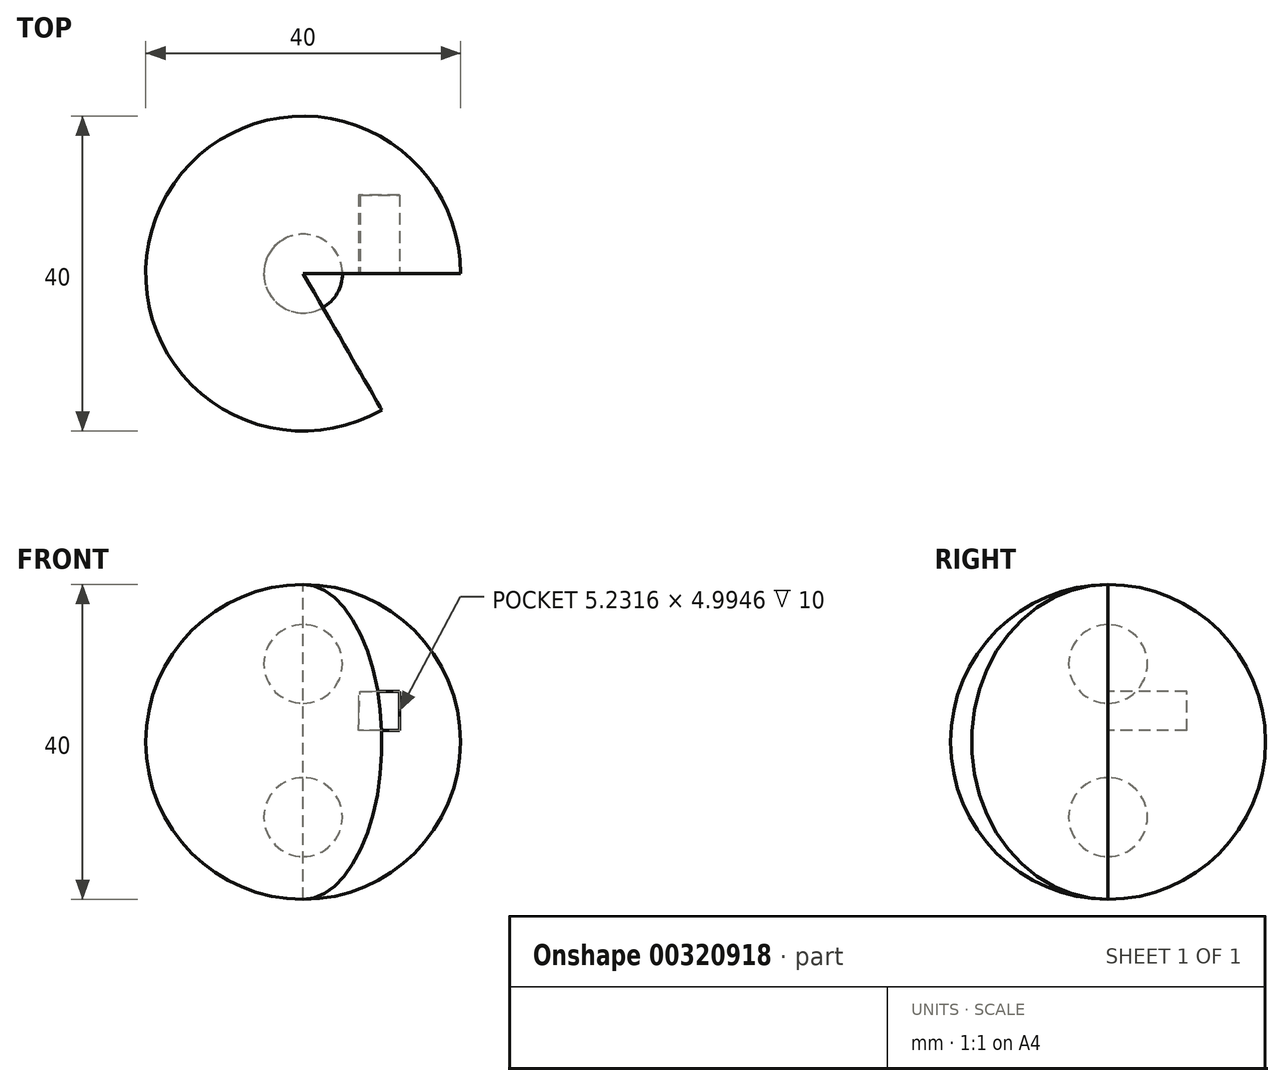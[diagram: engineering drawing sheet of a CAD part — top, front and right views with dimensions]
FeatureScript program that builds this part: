
annotation { "Feature Type Name" : "Feature", "Feature Type Description" : "" }
export const myFeature = defineFeature(function(context is Context, id is Id, definition is map)
    precondition{}
    {
        {
            var Q0;
            Q0=qCreatedBy(makeId("Front.planeOp"),FACE);
            var sketch = newSketch(context, id + "F0", { "sketchPlane" : qUnion([Q0])});
            skLineSegment(sketch, "E0", {"start": v(0, 0) * mm, "end": v(0, 40) * mm});
            skArc(sketch, "E1", {"start": v(0, 0) * mm, "mid": v(20, 20) * mm, "end": v(0, 40) * mm});
            skSolve(sketch);
        }
        {
            var Q0;
            Q0=makeQuery(id+"F0.imprint","IMPRINT",FACE,{"disambiguationData":[TD([[makeQuery(id+"F0.imprint","IMPRINT",EDGE,{"derivedFrom":sQuery(id+"F0.wireOp",EDGE,"E0")}),-1.0]])]});
            var Q1;
            Q1=sQuery(id+"F0.wireOp",EDGE,"E0");
            revolve(context, id + "F1", {"entities" : qUnion([Q0]), "axis" : qUnion([Q1]), "revolveType" : RevolveType.ONE_DIRECTION, "angle" : 300 * degree});
        }
        {
            var Q0;
            Q0=makeQuery(id+"F1.opRevolve","CAP_FACE",FACE,{"disambiguationData":[OSD([sQuery(id+"F0.wireOp",EDGE,"E0"),sQuery(id+"F0.wireOp",EDGE,"E1")])],"isStart":true});
            var sketch = newSketch(context, id + "F2", { "sketchPlane" : qUnion([Q0])});
            skLineSegment(sketch, "E2", {"start": v(7.24, 26.44) * mm, "end": v(12.24, 26.44) * mm});
            skLineSegment(sketch, "E3", {"start": v(12.24, 26.44) * mm, "end": v(12.24, 21.44) * mm});
            skLineSegment(sketch, "E4", {"start": v(12.24, 21.44) * mm, "end": v(7, 21.44) * mm});
            skLineSegment(sketch, "E5", {"start": v(7, 21.44) * mm, "end": v(7.24, 26.44) * mm});
            skSolve(sketch);
        }
        {
            var Q0;
            Q0 = qSketchRegion(id + "F2", true);
            extrude(context, id + "F3", {"entities" : qUnion([Q0]), "operationType" : NewBodyOperationType.REMOVE, "oppositeDirection" : true, "depth" : 10 * mm});
        }
        {
            var Q0;
            Q0=makeQuery(id+"F0.imprint","IMPRINT",FACE,{"disambiguationData":[TD([[makeQuery(id+"F0.imprint","IMPRINT",EDGE,{"derivedFrom":sQuery(id+"F0.wireOp",EDGE,"E0")}),-1.0]])]});
            var sketch = newSketch(context, id + "F4", { "sketchPlane" : qUnion([Q0])});
            skLineSegment(sketch, "E6", {"start": v(0, 15.45) * mm, "end": v(0, 5.45) * mm});
            skArc(sketch, "E7", {"start": v(0, 5.45) * mm, "mid": v(5, 10.45) * mm, "end": v(0, 15.45) * mm});
            skSolve(sketch);
        }
        {
            var Q0;
            Q0 = qSketchRegion(id + "F4", true);
            var Q1;
            Q1=sQuery(id+"F0.wireOp",EDGE,"E0");
            revolve(context, id + "F5", {"entities" : qUnion([Q0]), "axis" : qUnion([Q1]), "revolveType" : RevolveType.FULL});
        }
        {
            var Q0;
            Q0=makeQuery(id+"F1.opRevolve","CAP_FACE",FACE,{"disambiguationData":[OSD([sQuery(id+"F0.wireOp",EDGE,"E0"),sQuery(id+"F0.wireOp",EDGE,"E1")])],"isStart":false});
            var sketch = newSketch(context, id + "F6", { "sketchPlane" : qUnion([Q0])});
            skLineSegment(sketch, "E8", {"start": v(0, 34.91) * mm, "end": v(0, 24.91) * mm});
            skArc(sketch, "E9", {"start": v(0, 34.91) * mm, "mid": v(-5, 29.91) * mm, "end": v(0, 24.91) * mm});
            skSolve(sketch);
        }
        {
            var Q0;
            Q0 = qSketchRegion(id + "F6", true);
            var Q1;
            Q1=sQuery(id+"F0.wireOp",EDGE,"E0");
            revolve(context, id + "F7", {"entities" : qUnion([Q0]), "axis" : qUnion([Q1]), "revolveType" : RevolveType.FULL});
        }
    });
